FCSTD DOCUMENT  (FreeCAD 1.1R38827 (Git))
Label: composit_stand3_tech_sector_hor_main
License: All rights reserved
LicenseURL: http://en.wikipedia.org/wiki/All_rights_reserved
objects: PartDesign::SubShapeBinder×2, App::Link×2, Part::FeaturePython×1, Sketcher::SketchObject×1
note: 5 computed .brp shape members not serialized (recipe doc carries the construction recipe); baked Part::Feature solids carry a one-line shape summary decoded from their .brp
EXTERNAL_REF file=composit_stand3_tech_sector_plexiglass_main.FCStd obj=Sketch
EXTERNAL_REF file=composit_stand3_tech_sector_pillar_main.FCStd obj=Sketch
EXTERNAL_REF file=composit_stand3_tech_sector_plexiglass_main.FCStd obj=Placment
EXTERNAL_REF file=composit_stand3_tech_sector_pillar_main.FCStd obj=Placment

FEATURE [PartDesign::SubShapeBinder] Binder
  BindCopyOnChange = 0
  BindMode = 0
  ClaimChildren = false
  Fuse = false
  MakeFace = true
  OffsetFill = false
  OffsetIntersection = false
  OffsetJoinType = 0
  OffsetOpenResult = false
  PartialLoad = false
  Relative = true
  Support = -> [<external composit_stand3_tech_sector_plexiglass_main.FCStd>#Sketch]
  _Version = 2
FEATURE [PartDesign::SubShapeBinder] Binder001
  BindCopyOnChange = 0
  BindMode = 0
  ClaimChildren = false
  Fuse = false
  MakeFace = true
  OffsetFill = false
  OffsetIntersection = false
  OffsetJoinType = 0
  OffsetOpenResult = false
  PartialLoad = false
  Relative = true
  Support = -> [<external composit_stand3_tech_sector_pillar_main.FCStd>#Sketch]
  _Version = 2
FEATURE [App::Link] Link  label="edge_placement"
  LinkTransform = true
  LinkedObject = -> <external composit_stand3_tech_sector_plexiglass_main.FCStd>#Placment
FEATURE [App::Link] Link001  label="front_support_intersection_placement"
  LinkTransform = true
  LinkedObject = -> <external composit_stand3_tech_sector_pillar_main.FCStd>#Placment
FEATURE [Part::FeaturePython] Populate  label="Populate edge_placement with Binder001"  # WARN: FeaturePython — macro-defined, semantics opaque (R4)
  Copying = 0
  ExposePlacement = false
  MarkerShape = 1
  MarkerSize = 0
  NumElements = 0
  Object = -> Binder001
  OutputCompounding = 2
  PlacementsFrom = -> Link001
  PlacementsTo = -> Link
  Referencing = 3
  Type = lattice2PopulateCopies.LatticePopulateCopies
  isLattice = 0
FEATURE [Sketcher::SketchObject] Sketch
  ArcFitTolerance = 0
  ExternalGeometry = -> [Binder,Populate]
  FullyConstrained = true
  MakeInternals = false
  sketch-geometry (6):
    g0: ArcOfCircle CenterX=-383.193 CenterY=0 CenterZ=0 NormalX=0 NormalY=0 NormalZ=1 AngleXU=0 Radius=628.213 StartAngle=0 EndAngle=0.369284
    g1: ArcOfCircle CenterX=179.86 CenterY=276.175 CenterZ=0 NormalX=0 NormalY=0 NormalZ=1 AngleXU=0 Radius=3 StartAngle=0.377243 EndAngle=2.61799
    g2: ArcOfCircle CenterX=156.28 CenterY=235.332 CenterZ=0 NormalX=0 NormalY=0 NormalZ=1 AngleXU=0 Radius=3 StartAngle=2.61799 EndAngle=3.61477
    g3: ArcOfCircle CenterX=-303.381 CenterY=0 CenterZ=0 NormalX=0 NormalY=0 NormalZ=1 AngleXU=0 Radius=513.4 StartAngle=0 EndAngle=0.473178
    g4: LineSegment StartX=202.67 StartY=226.752 StartZ=0 EndX=182.65 EndY=277.28 EndZ=0
    g5: LineSegment StartX=153.682 StartY=236.832 StartZ=0 EndX=177.262 EndY=277.675 EndZ=0
  constraints (18):
    c: PointOnObject(g0,g-1)
    c: PointOnObject(g0,g-1)
    c: PointOnObject(g-3,g0)
    c: Coincident(g0,g-3)
    c: PointOnObject(g3,g-1)
    c: PointOnObject(g3,g-1)
    c: Coincident(g4,g0)
    c: Tangent(g4,g-3)
    c: Tangent(g4,g1) = -1.5708
    c: Tangent(g3,g2) = 1.5708
    c: Tangent(g5,g2) = 1.5708
    c: Tangent(g5,g1) = 1.5708
    c: PointOnObject(g-4,g5)
    c: PointOnObject(g2,g-4)
    c: Equal(g1,g2)
    c: Radius(g1) = 3
    c: PointOnObject(g-4,g3)
    c: DistanceX(g3,g0) = 35

RESOLVED EXTERNAL PARTS (link-assembly join: the EXTERNAL_REF files above that resolve inside this repo's crawl, each included once):
---- part composit_stand3_tech_sector_plexiglass_main.FCStd = doc fcstd_4438cd22ccd8 ----
FCSTD DOCUMENT  (FreeCAD 1.1R38827 (Git))
Label: composit_stand3_tech_sector_plexiglass_main
License: All rights reserved
LicenseURL: http://en.wikipedia.org/wiki/All_rights_reserved
objects: Part::FeaturePython×2, Sketcher::SketchObject×1, Part::Feature×1
note: 5 computed .brp shape members not serialized (recipe doc carries the construction recipe); baked Part::Feature solids carry a one-line shape summary decoded from their .brp
EXTERNAL_REF file=composit_stand3_tech_sector_pillar_main.FCStd obj=Sketch

FEATURE [Sketcher::SketchObject] Sketch  label="main_sketch"
  ArcFitTolerance = 0
  FullyConstrained = true
  MakeInternals = false
  expr: .Constraints.angle = 60 deg + <<composit_stand3_tech_sector_pillar_main>>#<<Sketch>>.Constraints.angle
  expr: Constraints[5] = <<composit_stand3_tech_sector_pillar_main>>#<<Sketch>>.Constraints.front
  sketch-geometry (3):
    g0: LineSegment StartX=202.67 StartY=226.752 StartZ=0 EndX=180.364 EndY=283.047 EndZ=0
    g1: ArcOfCircle CenterX=-357 CenterY=5 CenterZ=0 NormalX=0 NormalY=0 NormalZ=1 AngleXU=0 Radius=602 StartAngle=0 EndAngle=0.377243
    g2: LineSegment StartX=245 StartY=5 StartZ=0 EndX=245 EndY=0 EndZ=0
  constraints (9):
    c: Angle(g0) = 1.94804  'angle'
    c: Tangent(g0,g1) = -1.5708
    c: Vertical(g2)
    c: Tangent(g2,g1) = 1.5708
    c: DistanceY(g2,g2) = 5
    c: Distance(g0) = 60.5533
    c: PointOnObject(g2,g-1)
    c: Radius(g1) = 602  'r'
    c: DistanceX(g2) = 245  'offset'
FEATURE [Part::Feature] Body160  label="tech_sector_plexiglass_material_0.30ansi001"
  Placement = pos=(0,0,0) rot=(0,0,-1;0.523599rad)
  shape: bbox 73.31 x 566.4 x 419 mm, 26 faces (baked)
FEATURE [Part::FeaturePython] Placment  label="edge_placement"  # WARN: FeaturePython — macro-defined, semantics opaque (R4)
  AttacherType = Attacher::AttachEngine3D
  AttachmentOffset = pos=(0,0,0) rot=(-0.57735,0.57735,0.57735;2.0944rad)
  AttachmentSupport = -> [Sketch]
  ExposePlacement = true
  MapMode = 7
  MarkerShape = 1
  MarkerSize = 50
  NumElements = 1
  Placement = pos=(180.364,283.047,0) rot=(0,0,1;1.94804rad)
  Type = lattice2AttachablePlacement.AttachablePlacement
  isLattice = 1
FEATURE [Part::FeaturePython] Placment001  label="fix_corner_placement"  # WARN: FeaturePython — macro-defined, semantics opaque (R4)
  AttacherType = Attacher::AttachEngine3D
  ExposePlacement = true
  MarkerShape = 1
  MarkerSize = 200
  NumElements = 1
  Placement = pos=(245,0,3) rot=(0,0,1;1.5708rad)
  Type = lattice2AttachablePlacement.AttachablePlacement
  isLattice = 1
  expr: .Placement.Base.x = <<main_sketch>>.Constraints.offset
